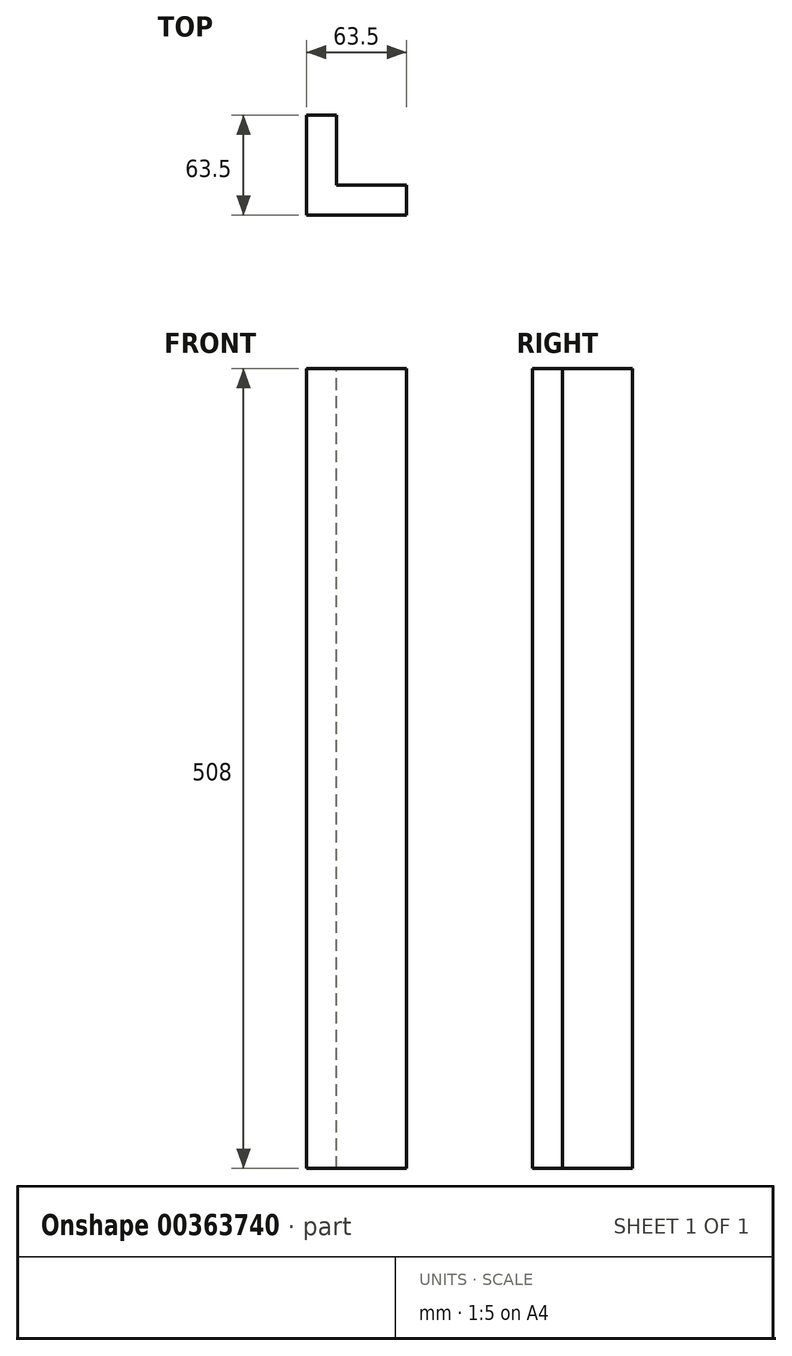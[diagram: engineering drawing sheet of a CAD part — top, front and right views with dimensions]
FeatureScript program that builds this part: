
annotation { "Feature Type Name" : "Feature", "Feature Type Description" : "" }
export const myFeature = defineFeature(function(context is Context, id is Id, definition is map)
    precondition{}
    {
        {
            var Q0;
            Q0=qCreatedBy(makeId("Front.planeOp"),FACE);
            var sketch = newSketch(context, id + "F0", { "sketchPlane" : qUnion([Q0])});
            skLineSegment(sketch, "E0.bottom", {"start": v(31.75, -254) * mm, "end": v(-31.75, -254) * mm});
            skLineSegment(sketch, "E0.top", {"start": v(31.75, 254) * mm, "end": v(-31.75, 254) * mm});
            skLineSegment(sketch, "E0.left", {"start": v(31.75, -254) * mm, "end": v(31.75, 254) * mm});
            skLineSegment(sketch, "E0.right", {"start": v(-31.75, -254) * mm, "end": v(-31.75, 254) * mm});
            skPoint(sketch, "E0.middle", {"position": v(0, 0) * mm});
            skSolve(sketch);
        }
        {
            var Q0;
            Q0 = qSketchRegion(id + "F0", true);
            extrude(context, id + "F1", {"entities" : qUnion([Q0]), "depth" : 19.05 * mm});
        }
        {
            var Q0;
            Q0=makeQuery(id+"F1.opExtrude","SWEPT_FACE",FACE,{"disambiguationData":[OSD([sQuery(id+"F0.wireOp",EDGE,"E0.right")])]});
            var sketch = newSketch(context, id + "F2", { "sketchPlane" : qUnion([Q0])});
            skLineSegment(sketch, "E1.bottom", {"start": v(0, 254) * mm, "end": v(-44.45, 254) * mm});
            skLineSegment(sketch, "E1.top", {"start": v(0, -254) * mm, "end": v(-44.45, -254) * mm});
            skLineSegment(sketch, "E1.left", {"start": v(0, 254) * mm, "end": v(0, -254) * mm});
            skLineSegment(sketch, "E1.right", {"start": v(-44.45, 254) * mm, "end": v(-44.45, -254) * mm});
            skSolve(sketch);
        }
        {
            var Q0;
            Q0 = qSketchRegion(id + "F2", true);
            extrude(context, id + "F3", {"entities" : qUnion([Q0]), "operationType" : NewBodyOperationType.ADD, "oppositeDirection" : true, "depth" : 19.05 * mm});
        }
    });
